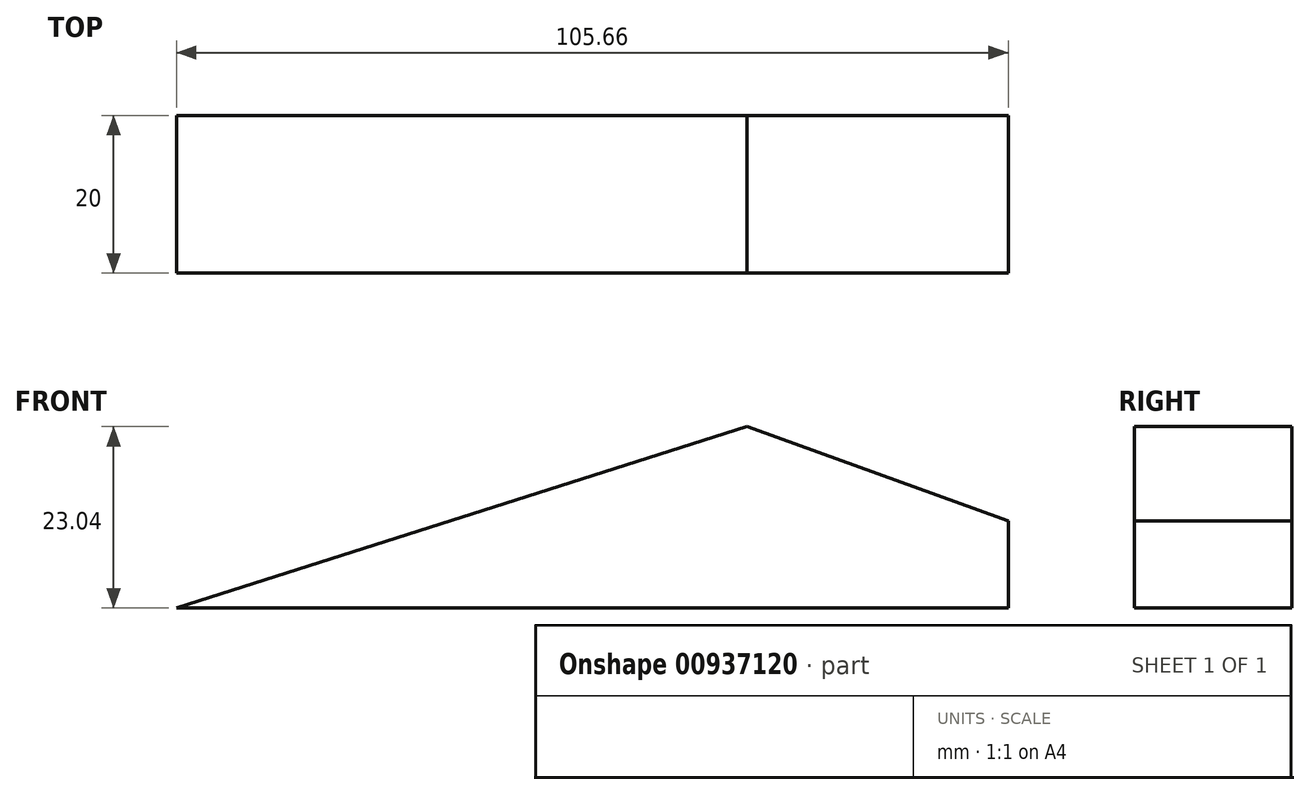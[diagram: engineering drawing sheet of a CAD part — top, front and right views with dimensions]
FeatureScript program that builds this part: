
annotation { "Feature Type Name" : "Feature", "Feature Type Description" : "" }
export const myFeature = defineFeature(function(context is Context, id is Id, definition is map)
    precondition{}
    {
        {
            var Q0;
            Q0=qCreatedBy(makeId("Front.planeOp"),FACE);
            var sketch = newSketch(context, id + "F0", { "sketchPlane" : qUnion([Q0])});
            skLineSegment(sketch, "E0", {"start": v(-45.61, 0) * mm, "end": v(60.05, 0) * mm});
            skLineSegment(sketch, "E1", {"start": v(60.05, 0) * mm, "end": v(60.05, 11.06) * mm});
            skLineSegment(sketch, "E2", {"start": v(60.05, 11.06) * mm, "end": v(26.87, 23.04) * mm});
            skLineSegment(sketch, "E3", {"start": v(26.87, 23.04) * mm, "end": v(-45.61, 0) * mm});
            skSolve(sketch);
        }
        {
            var Q0;
            Q0=makeQuery(id+"F0.imprint","IMPRINT",FACE,{"disambiguationData":[TD([[makeQuery(id+"F0.imprint","IMPRINT",EDGE,{"derivedFrom":sQuery(id+"F0.wireOp",EDGE,"E0")}),1.0]])]});
            extrude(context, id + "F1", {"entities" : qUnion([Q0]), "depth" : 20 * mm, "offsetDistance" : 25.4 * mm});
        }
    });
